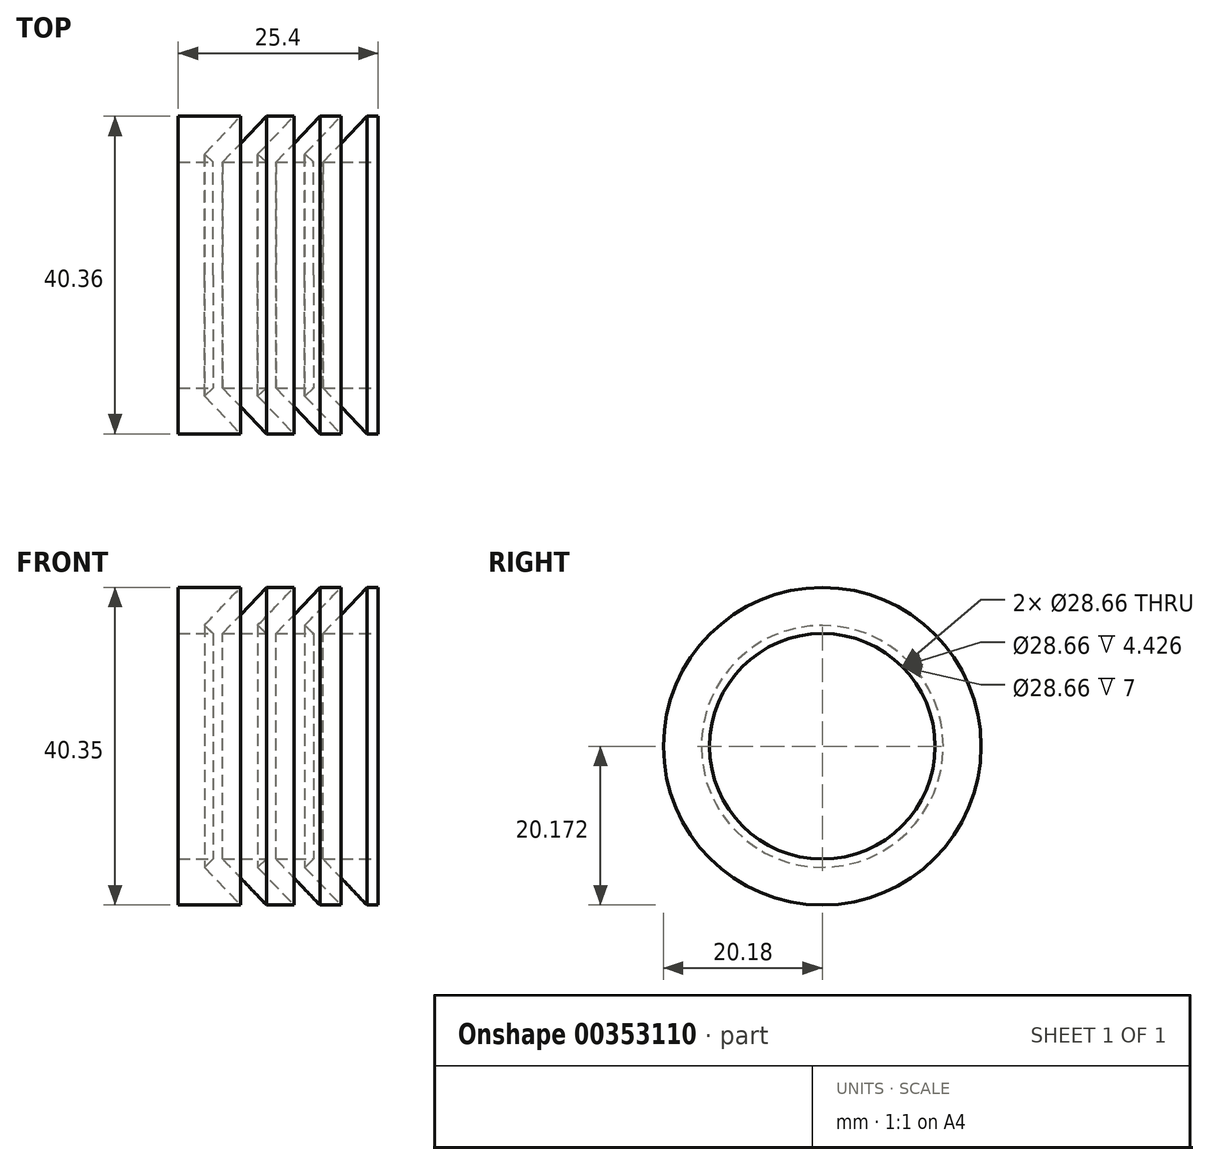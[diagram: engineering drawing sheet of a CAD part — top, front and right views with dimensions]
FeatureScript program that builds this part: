
annotation { "Feature Type Name" : "Feature", "Feature Type Description" : "" }
export const myFeature = defineFeature(function(context is Context, id is Id, definition is map)
    precondition{}
    {
        {
            var Q0;
            Q0=qCreatedBy(makeId("Front.planeOp"),FACE);
            var sketch = newSketch(context, id + "F0", { "sketchPlane" : qUnion([Q0])});
            skLineSegment(sketch, "E0.bottom", {"start": v(-12.7, 10.09) * mm, "end": v(-4.78, 10.09) * mm});
            skLineSegment(sketch, "E0.left", {"start": v(-12.7, 10.09) * mm, "end": v(-12.7, -8.96) * mm});
            skLineSegment(sketch, "E0.right", {"start": v(12.7, 10.09) * mm, "end": v(12.7, -8.96) * mm});
            skLineSegment(sketch, "E1", {"start": v(-4.78, 10.09) * mm, "end": v(-9.37, 5.28) * mm});
            skLineSegment(sketch, "E2", {"start": v(-9.37, 5.28) * mm, "end": v(-7.64, 3.63) * mm});
            skLineSegment(sketch, "E3", {"start": v(-7.64, 3.63) * mm, "end": v(-1.48, 10.09) * mm});
            skLineSegment(sketch, "E4", {"start": v(2, 10.09) * mm, "end": v(-2.6, 5.28) * mm});
            skLineSegment(sketch, "E5", {"start": v(-2.6, 5.28) * mm, "end": v(-0.86, 3.63) * mm});
            skLineSegment(sketch, "E6", {"start": v(-0.86, 3.63) * mm, "end": v(5.3, 10.09) * mm});
            skLineSegment(sketch, "E7", {"start": v(7.97, 10.09) * mm, "end": v(3.39, 5.28) * mm});
            skLineSegment(sketch, "E8", {"start": v(3.39, 5.28) * mm, "end": v(5.12, 3.63) * mm});
            skLineSegment(sketch, "E9", {"start": v(5.12, 3.63) * mm, "end": v(11.28, 10.09) * mm});
            skLineSegment(sketch, "E10.MirrorCS", {"start": v(-4.78, -10.09) * mm, "end": v(-9.37, -5.28) * mm});
            skLineSegment(sketch, "E11.MirrorCS", {"start": v(-7.64, -3.63) * mm, "end": v(-1.48, -10.09) * mm});
            skLineSegment(sketch, "E12.MirrorCS", {"start": v(-9.37, -5.28) * mm, "end": v(-7.64, -3.63) * mm});
            skLineSegment(sketch, "E13.MirrorCS", {"start": v(-2.6, -5.28) * mm, "end": v(-0.86, -3.63) * mm});
            skLineSegment(sketch, "E14.MirrorCS", {"start": v(2, -10.09) * mm, "end": v(-2.6, -5.28) * mm});
            skLineSegment(sketch, "E15.MirrorCS", {"start": v(-0.86, -3.63) * mm, "end": v(5.3, -10.09) * mm});
            skLineSegment(sketch, "E16.MirrorCS", {"start": v(7.97, -10.09) * mm, "end": v(3.39, -5.28) * mm});
            skLineSegment(sketch, "E17.MirrorCS", {"start": v(5.12, -3.63) * mm, "end": v(11.28, -10.09) * mm});
            skLineSegment(sketch, "E18.MirrorCS", {"start": v(3.39, -5.28) * mm, "end": v(5.12, -3.63) * mm});
            skLineSegment(sketch, "E19.trimOffspring", {"start": v(11.28, 10.09) * mm, "end": v(12.7, 10.09) * mm});
            skLineSegment(sketch, "E20", {"start": v(-12.7, -8.96) * mm, "end": v(-12.7, -10.09) * mm});
            skLineSegment(sketch, "E21", {"start": v(-12.7, -10.09) * mm, "end": v(-4.78, -10.09) * mm});
            skLineSegment(sketch, "E22", {"start": v(12.7, -10.09) * mm, "end": v(12.7, -8.96) * mm});
            skLineSegment(sketch, "E23.trimOffspring", {"start": v(5.3, -10.09) * mm, "end": v(7.97, -10.09) * mm});
            skLineSegment(sketch, "E24.trimOffspring", {"start": v(11.28, -10.09) * mm, "end": v(12.7, -10.09) * mm});
            skLineSegment(sketch, "E25", {"start": v(-1.48, -10.09) * mm, "end": v(2, -10.09) * mm});
            skLineSegment(sketch, "E26", {"start": v(-1.48, 10.09) * mm, "end": v(2, 10.09) * mm});
            skLineSegment(sketch, "E27", {"start": v(5.3, 10.09) * mm, "end": v(7.97, 10.09) * mm});
            skPoint(sketch, "E28.end.orphan", {"position": v(19.46, 10.09) * mm});
            skSolve(sketch);
        }
        {
            var Q0;
            Q0=makeQuery(id+"F0.imprint","IMPRINT",FACE,{"disambiguationData":[TD([[makeQuery(id+"F0.imprint","IMPRINT",EDGE,{"derivedFrom":sQuery(id+"F0.wireOp",EDGE,"E0.bottom")}),-1.0]])]});
            var Q1;
            Q1=sQuery(id+"F0.wireOp",EDGE,"E24.trimOffspring");
            revolve(context, id + "F1", {"entities" : qUnion([Q0]), "axis" : qUnion([Q1]), "revolveType" : RevolveType.FULL});
        }
        {
            var Q0;
            Q0=makeQuery(id+"F1.opRevolve","SWEPT_FACE",FACE,{"disambiguationData":[OSD([sQuery(id+"F0.wireOp",EDGE,"E0.right"),sQuery(id+"F0.wireOp",EDGE,"E22")])]});
            var sketch = newSketch(context, id + "F2", { "sketchPlane" : qUnion([Q0])});
            skCircle(sketch, "E29", {"center": v(0, -10.09) * mm, "radius": 14.33 * mm});
            skSolve(sketch);
        }
        {
            var Q0;
            Q0=makeQuery(id+"F2.imprint","IMPRINT",FACE,{"disambiguationData":[TD([[makeQuery(id+"F2.imprint","IMPRINT",EDGE,{"derivedFrom":sQuery(id+"F2.wireOp",EDGE,"E29")}),1.0]])]});
            extrude(context, id + "F3", {"entities" : qUnion([Q0]), "operationType" : NewBodyOperationType.REMOVE, "oppositeDirection" : true, "depth" : 254 * mm});
        }
    });
